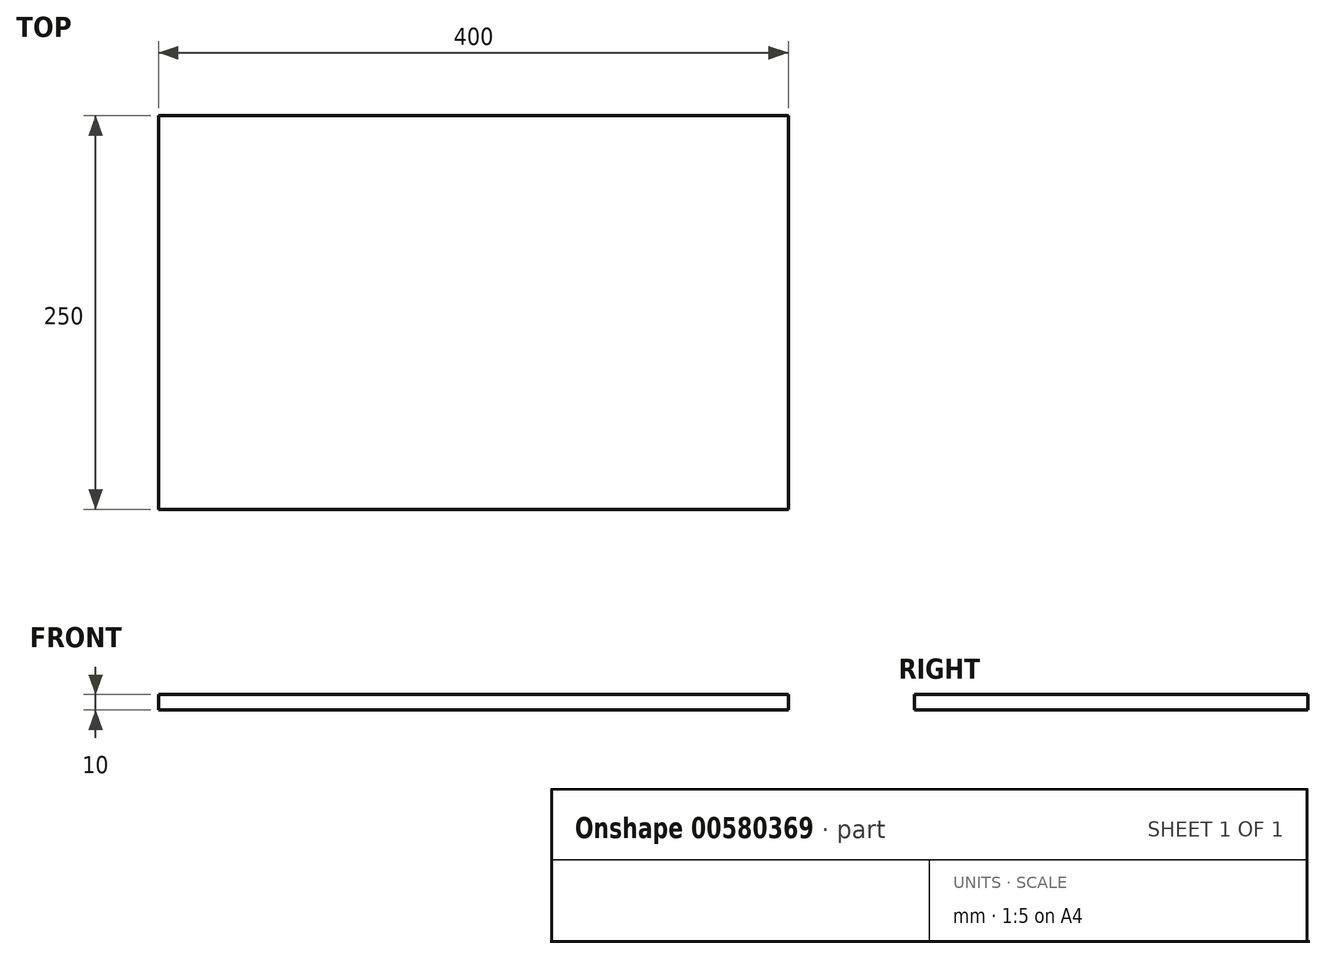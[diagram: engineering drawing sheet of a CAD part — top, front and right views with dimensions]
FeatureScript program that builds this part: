
annotation { "Feature Type Name" : "Feature", "Feature Type Description" : "" }
export const myFeature = defineFeature(function(context is Context, id is Id, definition is map)
    precondition{}
    {
        {
            var Q0;
            Q0=qCreatedBy(makeId("Top.planeOp"),FACE);
            var sketch = newSketch(context, id + "F0", { "sketchPlane" : qUnion([Q0])});
            skLineSegment(sketch, "E0.bottom", {"start": v(200, 125) * mm, "end": v(-200, 125) * mm});
            skLineSegment(sketch, "E0.top", {"start": v(200, -125) * mm, "end": v(-200, -125) * mm});
            skLineSegment(sketch, "E0.left", {"start": v(200, 125) * mm, "end": v(200, -125) * mm});
            skLineSegment(sketch, "E0.right", {"start": v(-200, 125) * mm, "end": v(-200, -125) * mm});
            skPoint(sketch, "E0.middle", {"position": v(0, 0) * mm});
            skSolve(sketch);
        }
        {
            var Q0;
            Q0=makeQuery(id+"F0.imprint","IMPRINT",FACE,{"disambiguationData":[TD([[makeQuery(id+"F0.imprint","IMPRINT",EDGE,{"derivedFrom":sQuery(id+"F0.wireOp",EDGE,"E0.bottom")}),1.0]])]});
            extrude(context, id + "F1", {"entities" : qUnion([Q0]), "depth" : 10 * mm, "offsetDistance" : 25 * mm});
        }
    });
